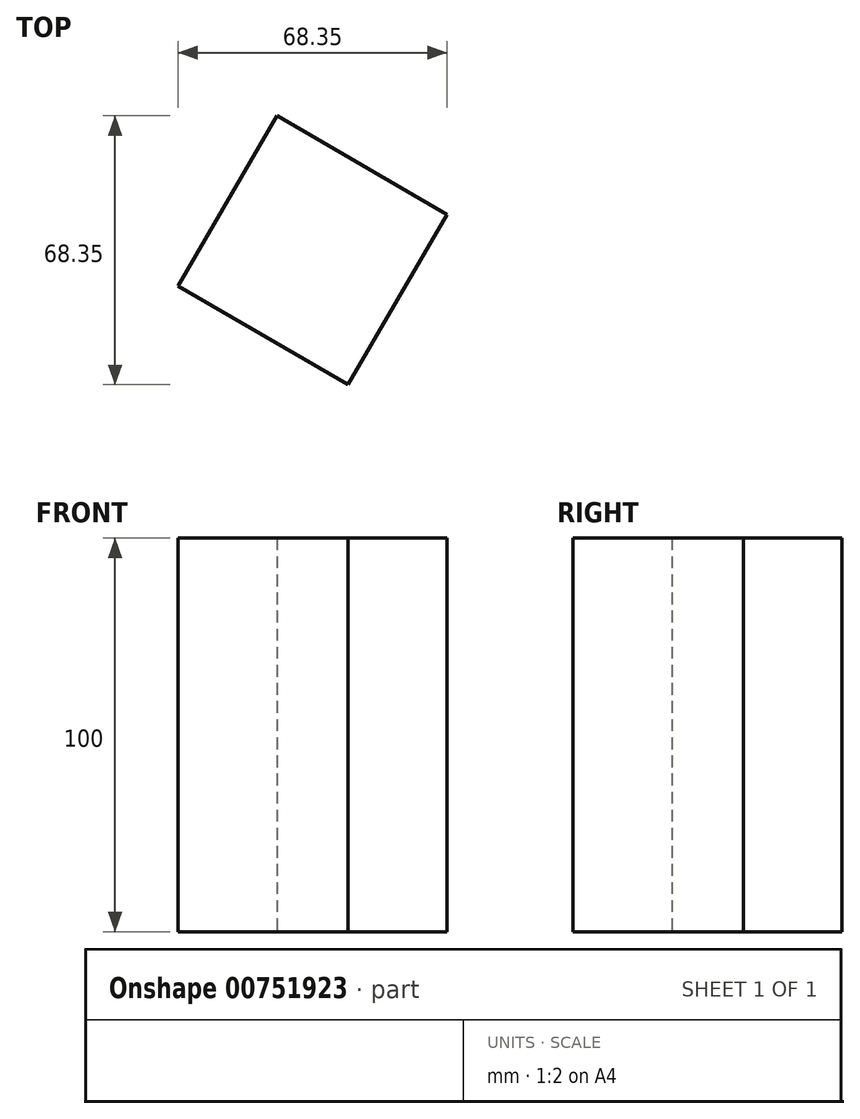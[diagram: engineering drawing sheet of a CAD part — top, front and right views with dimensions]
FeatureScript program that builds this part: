
annotation { "Feature Type Name" : "Feature", "Feature Type Description" : "" }
export const myFeature = defineFeature(function(context is Context, id is Id, definition is map)
    precondition{}
    {
        {
            var Q0;
            Q0=qCreatedBy(makeId("Top.planeOp"),FACE);
            var sketch = newSketch(context, id + "F0", { "sketchPlane" : qUnion([Q0])});
            skCircle(sketch, "E0.cCircle", {"center": v(0, 0) * mm, "radius": 29.48 * mm, "construction": true});
            skLineSegment(sketch, "E0.0", {"start": v(-40.3, -10.68) * mm, "end": v(-10.68, 40.3) * mm});
            skLineSegment(sketch, "E0.1", {"start": v(-10.68, 40.3) * mm, "end": v(40.3, 10.68) * mm});
            skLineSegment(sketch, "E0.2", {"start": v(40.3, 10.68) * mm, "end": v(10.68, -40.3) * mm});
            skLineSegment(sketch, "E0.3", {"start": v(10.68, -40.3) * mm, "end": v(-40.3, -10.68) * mm});
            skPoint(sketch, "E0.0.midPoint", {"position": v(-25.5, 14.81) * mm});
            skSolve(sketch);
        }
        {
            var Q0;
            Q0=makeQuery(id+"F0.imprint","IMPRINT",FACE,{"disambiguationData":[TD([[makeQuery(id+"F0.imprint","IMPRINT",EDGE,{"derivedFrom":sQuery(id+"F0.wireOp",EDGE,"E0.0")}),-1.0]])]});
            extrude(context, id + "F1", {"entities" : qUnion([Q0]), "depth" : 100 * mm, "offsetDistance" : 25 * mm});
        }
        {
            var Q0;
            Q0=makeQuery(id+"F1.opExtrude","SWEPT_FACE",FACE,{"disambiguationData":[OSD([sQuery(id+"F0.wireOp",EDGE,"E0.0")])]});
            extrude(context, id + "F2", {"entities" : qUnion([Q0]), "operationType" : NewBodyOperationType.ADD, "depth" : -8.96 * mm, "offsetDistance" : 25 * mm});
        }
        {
            var Q0;
            Q0=makeQuery(id+"F1.opExtrude","SWEPT_FACE",FACE,{"disambiguationData":[OSD([sQuery(id+"F0.wireOp",EDGE,"E0.0")])]});
            extrude(context, id + "F3", {"entities" : qUnion([Q0]), "operationType" : NewBodyOperationType.REMOVE, "oppositeDirection" : true, "depth" : 8.96 * mm, "offsetDistance" : 25 * mm});
        }
        {
            var Q0;
            Q0=makeQuery(id+"F1.opExtrude","SWEPT_FACE",FACE,{"disambiguationData":[OSD([sQuery(id+"F0.wireOp",EDGE,"E0.3")])]});
            extrude(context, id + "F4", {"entities" : qUnion([Q0]), "operationType" : NewBodyOperationType.REMOVE, "oppositeDirection" : true, "depth" : 8.96 * mm, "offsetDistance" : 25 * mm});
        }
    });
